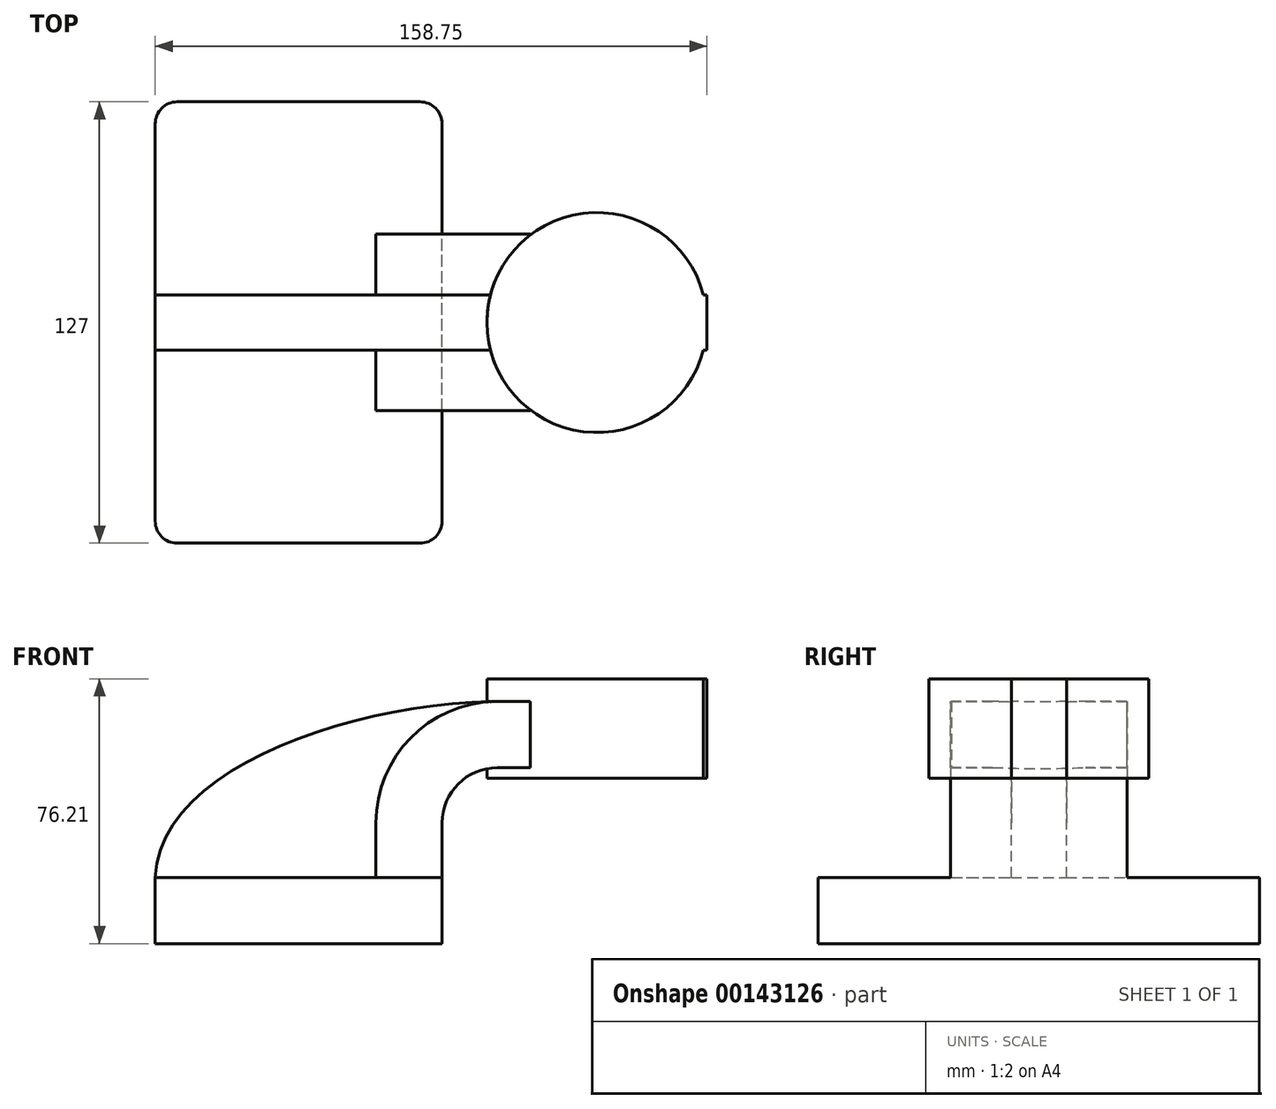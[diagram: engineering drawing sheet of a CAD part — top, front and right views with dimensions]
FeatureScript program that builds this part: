
annotation { "Feature Type Name" : "Feature", "Feature Type Description" : "" }
export const myFeature = defineFeature(function(context is Context, id is Id, definition is map)
    precondition{}
    {
        {
            var Q0;
            Q0=qCreatedBy(makeId("Front.planeOp"),FACE);
            var sketch = newSketch(context, id + "F0", { "sketchPlane" : qUnion([Q0])});
            skLineSegment(sketch, "E0.bottom", {"start": v(41.28, -9.53) * mm, "end": v(-41.27, -9.53) * mm});
            skLineSegment(sketch, "E0.top", {"start": v(41.27, 9.53) * mm, "end": v(-41.28, 9.52) * mm});
            skLineSegment(sketch, "E0.left", {"start": v(41.28, -9.52) * mm, "end": v(41.28, 9.53) * mm});
            skLineSegment(sketch, "E0.right", {"start": v(-41.28, -9.53) * mm, "end": v(-41.28, 9.52) * mm});
            skPoint(sketch, "E0.middle", {"position": v(0, 0) * mm});
            skLineSegment(sketch, "E1.bottom", {"start": v(117.47, 38.1) * mm, "end": v(66.67, 38.1) * mm});
            skLineSegment(sketch, "E1.top", {"start": v(117.47, 66.67) * mm, "end": v(66.67, 66.67) * mm});
            skLineSegment(sketch, "E1.left", {"start": v(117.47, 38.1) * mm, "end": v(117.47, 66.67) * mm});
            skLineSegment(sketch, "E1.right", {"start": v(66.67, 38.1) * mm, "end": v(66.67, 66.67) * mm});
            skPoint(sketch, "E1.middle", {"position": v(92.07, 52.39) * mm});
            skLineSegment(sketch, "E2", {"start": v(41.27, 9.53) * mm, "end": v(41.27, 25.2) * mm});
            skArc(sketch, "E3", {"start": v(57.15, 41.07) * mm, "mid": v(45.92, 36.42) * mm, "end": v(41.28, 25.2) * mm});
            skLineSegment(sketch, "E4", {"start": v(57.15, 41.07) * mm, "end": v(85.72, 41.07) * mm});
            skLineSegment(sketch, "E5.0", {"start": v(22.23, 9.53) * mm, "end": v(22.23, 25.2) * mm});
            skArc(sketch, "E5.1", {"start": v(57.15, 60.12) * mm, "mid": v(32.45, 49.9) * mm, "end": v(22.23, 25.2) * mm});
            skLineSegment(sketch, "E5.2", {"start": v(57.15, 60.12) * mm, "end": v(85.72, 60.12) * mm});
            skFitSpline(sketch, "E6", {"points": [v(-41.28, 9.52) * mm, v(57.15, 60.12) * mm], "startDerivative": vector(3.14, 95.29) * mm, "endDerivative": vector(122.6, 1.04) * mm});
            skLineSegment(sketch, "E7", {"start": v(85.83, 38.1) * mm, "end": v(85.83, 66.67) * mm});
            skSolve(sketch);
        }
        {
            var Q0;
            Q0=makeQuery(id+"F0.imprint","IMPRINT",FACE,{"disambiguationData":[TD([[makeQuery(id+"F0.imprint","IMPRINT",EDGE,{"derivedFrom":sQuery(id+"F0.wireOp",EDGE,"E0.bottom")}),-1.0]])]});
            extrude(context, id + "F1", {"entities" : qUnion([Q0]), "endBound" : BoundingType.SYMMETRIC, "depth" : 127 * mm});
        }
        {
            var Q0;
            {var subQ2=sQuery(id+"F0.wireOp",EDGE,"E2");Q0=makeQuery(id+"F0.imprint","IMPRINT",FACE,{"disambiguationData":[TD([[makeQuery(id+"F0.imprint","IMPRINT",EDGE,{"derivedFrom":subQ2}),1.0]])]});}
            extrude(context, id + "F2", {"entities" : qUnion([Q0]), "operationType" : NewBodyOperationType.ADD, "endBound" : BoundingType.SYMMETRIC, "depth" : 50.8 * mm});
        }
        {
            var Q0;
            Q0 = qSketchRegion(id + "F0", true);
            extrude(context, id + "F3", {"entities" : qUnion([Q0]), "operationType" : NewBodyOperationType.ADD, "endBound" : BoundingType.SYMMETRIC, "depth" : 15.88 * mm});
        }
        {
            var Q0;
            {var subQ0=sQuery(id+"F0.wireOp",EDGE,"E1.left");Q0=makeQuery(id+"F0.imprint","IMPRINT",FACE,{"disambiguationData":[TD([[makeQuery(id+"F0.imprint","IMPRINT",EDGE,{"derivedFrom":subQ0}),1.0]])]});}
            var Q1;
            Q1=sQuery(id+"F0.wireOp",EDGE,"E7");
            revolve(context, id + "F4", {"operationType" : NewBodyOperationType.ADD, "entities" : qUnion([Q0]), "axis" : qUnion([Q1]), "revolveType" : RevolveType.FULL});
        }
        {
            var Q0;
            Q0=makeQuery(id+"F1.opExtrude","CAP_EDGE",EDGE,{"disambiguationData":[OSD([sQuery(id+"F0.wireOp",EDGE,"E0.right")])],"isStart":false});
            var Q1;
            Q1=makeQuery(id+"F1.opExtrude","CAP_EDGE",EDGE,{"disambiguationData":[OSD([sQuery(id+"F0.wireOp",EDGE,"E0.left")])],"isStart":false});
            var Q2;
            Q2=makeQuery(id+"F1.opExtrude","CAP_EDGE",EDGE,{"disambiguationData":[OSD([sQuery(id+"F0.wireOp",EDGE,"E0.left")])],"isStart":true});
            var Q3;
            Q3=makeQuery(id+"F1.opExtrude","CAP_EDGE",EDGE,{"disambiguationData":[OSD([sQuery(id+"F0.wireOp",EDGE,"E0.right")])],"isStart":true});
            fillet(context, id + "F5", {"entities" : qUnion([Q0, Q1, Q2, Q3]), "radius" : 6.35 * mm, "tangentPropagation" : true, "allowEdgeOverflow" : false});
        }
    });
